# Revit family: 202_KWI-_
name_source: partatom
category: Air Terminals
units: mm (PartAtom-declared; Revit-internal decimal feet)

## family parameters
Always vertical = Yes
Cut with Voids When Loaded = No
Part Type = Normal
Room Calculation Point = Yes
Round Connector Dimension = Use Diameter
Shared = No
Work Plane-Based = No

## types (5) — shared parameters
B = 16 mm  [stored 0.0524934 ft]
B__ve = -16 mm  [stored -0.0524934 ft]
CL_Location_5000 = 5000 mm  [stored 16.4042 ft]
Description = AIR EXHAUST VALVE INSULATED
L_ARR = 400 mm  [stored 1.31234 ft]
Manufacturer = Alnor
QmdConnectorList = 201;D
URL = http://www.ventilation-alnor.co.uk
W_ARR = 400 mm  [stored 1.31234 ft]
XRefLineVPlnId = 7453
YRefLineVPlnId = 7456
magiPartTypeId = 202
magiProductFamilyId = KWI-*
zero-valued in all types: CLBTZ, H_ARR

## per-type parameters (varying)
| type | A | D | R |
| KWI-080 | 108 mm  [stored 0.354331 ft] | 80 mm | 40 mm  [stored 0.131234 ft] |
| KWI-200 | 240 mm | 200 mm | 100 mm  [stored 0.328084 ft] |
| KWI-160 | 193 mm | 160 mm | 80 mm  [stored 0.262467 ft] |
| KWI-125 | 162 mm | 125 mm | 63 mm |
| KWI-100 | 137 mm | 100 mm | 50 mm |

note: column(s) folded — value = type name in every type: MC Product Code, magiProductId

note: [stored X ft] marks values corroborated as IEEE doubles in the binary element streams (Revit-internal decimal feet)

## geometry (parser evidence)
native form markers: Blend x2, Sweep x2
no freeform markers — native parametric forms only
